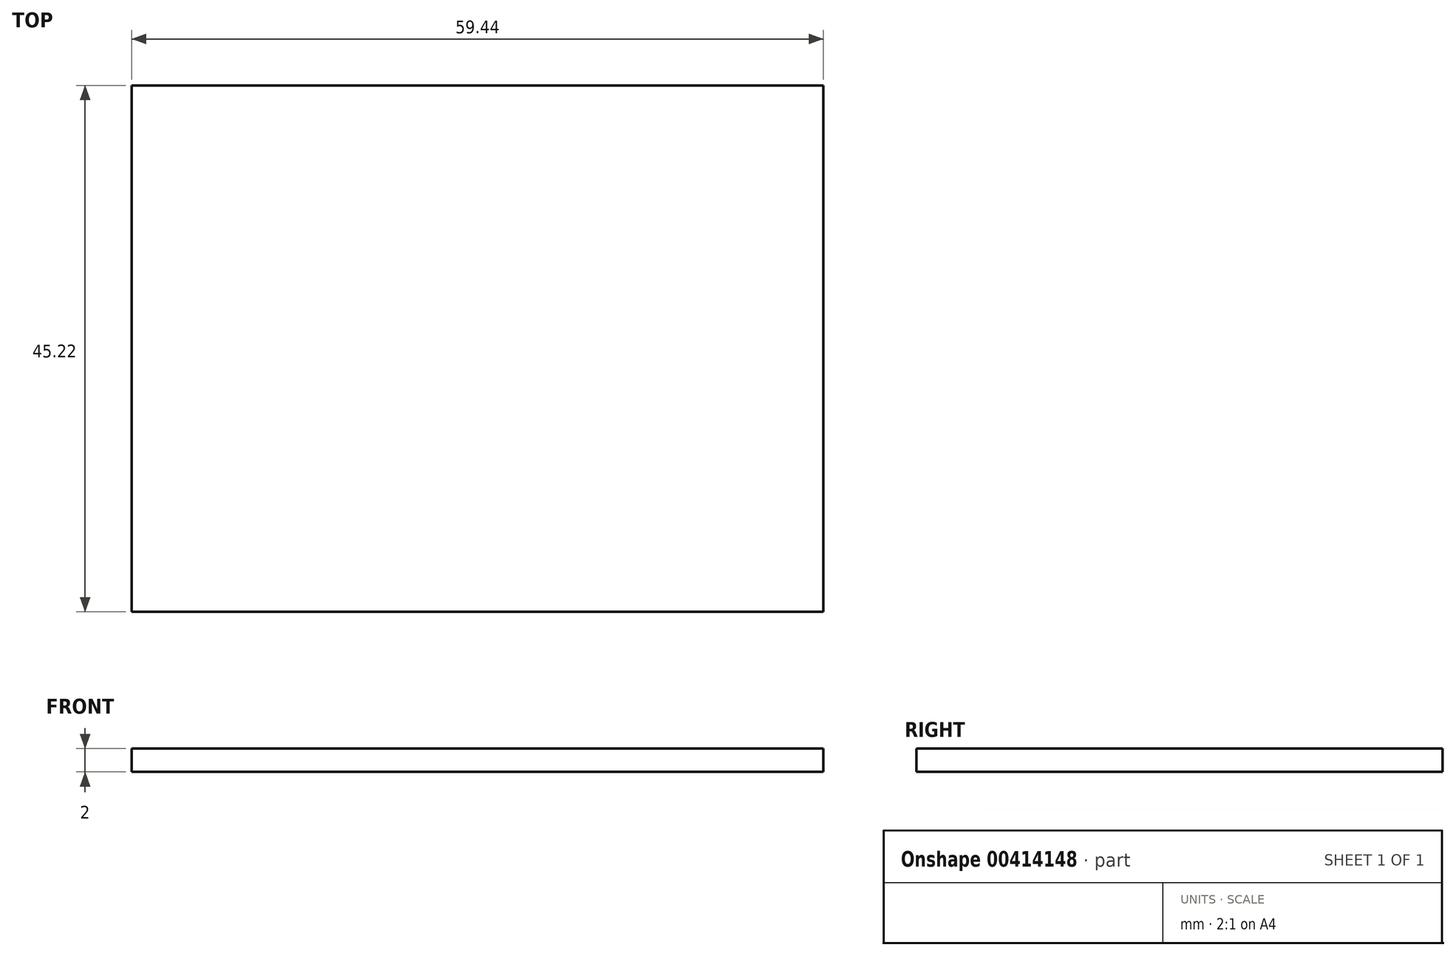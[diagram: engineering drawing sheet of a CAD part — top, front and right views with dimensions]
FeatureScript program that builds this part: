
annotation { "Feature Type Name" : "Feature", "Feature Type Description" : "" }
export const myFeature = defineFeature(function(context is Context, id is Id, definition is map)
    precondition{}
    {
        {
            var Q0;
            Q0=qCreatedBy(makeId("Top.planeOp"), FACE);
            var sketch = newSketch(context, id + "F0", { "sketchPlane" : qUnion([Q0])});
            skLineSegment(sketch, "E0.bottom", {"start": v(29.72, -22.6) * mm, "end": v(-29.72, -22.6) * mm});
            skLineSegment(sketch, "E0.top", {"start": v(29.72, 22.6) * mm, "end": v(-29.72, 22.6) * mm});
            skLineSegment(sketch, "E0.left", {"start": v(29.72, -22.6) * mm, "end": v(29.72, 22.6) * mm});
            skLineSegment(sketch, "E0.right", {"start": v(-29.72, -22.6) * mm, "end": v(-29.72, 22.6) * mm});
            skPoint(sketch, "E0.middle", {"position": v(0, 0) * mm});
            skSolve(sketch);
        }
        {
            var Q0;
            Q0 = qSketchRegion(id + "F0", true);
            extrude(context, id + "F1", {"entities" : qUnion([Q0]), "depth" : 2 * mm, "offsetDistance" : 25 * mm});
        }
    });
